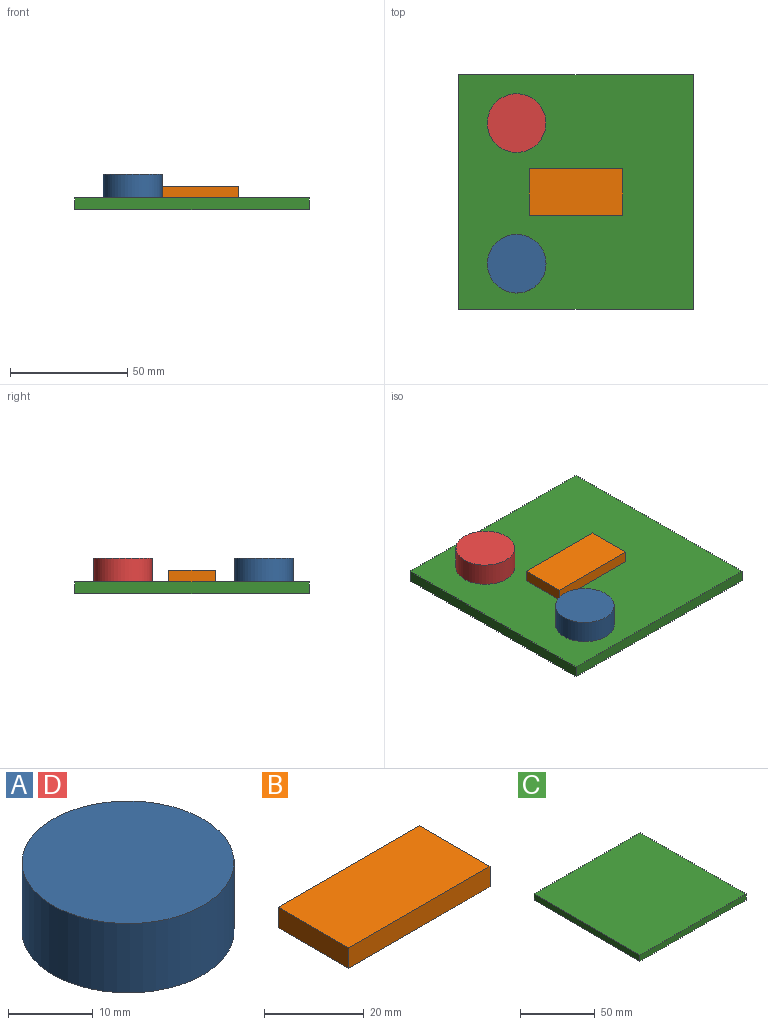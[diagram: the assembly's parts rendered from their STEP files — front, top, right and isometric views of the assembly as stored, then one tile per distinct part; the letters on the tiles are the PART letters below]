
ASSEMBLY  parts=4 mates=3
PART A: 3 faces, bbox 25x25x10 mm
  f0: cylinder r=12.5mm len=25mm, axis (0,0,-1), area 785.4mm2, adj f1,f2
  f1: plane 25x25mm, normal (0,0,1), area 490.9mm2, adj f0
  f2: plane 25x25mm, normal (0,0,-1), area 490.9mm2, adj f0
PART B: 6 faces, bbox 40x20x5 mm
  f0: plane 20x5mm, normal (1,0,0), area 100mm2, adj f1,f3,f4,f5
  f1: plane 40x5mm, normal (0,1,0), area 200mm2, adj f0,f2,f4,f5
  f2: plane 20x5mm, normal (-1,0,0), area 100mm2, adj f1,f3,f4,f5
  f3: plane 40x5mm, normal (0,-1,0), area 200mm2, adj f0,f2,f4,f5
  f4: plane 40x20mm, normal (0,0,1), area 800mm2, adj f0,f1,f2,f3
  f5: plane 40x20mm, normal (0,0,-1), area 800mm2, adj f0,f1,f2,f3
PART C: 6 faces, bbox 100x100x5 mm
  f0: plane 100x5mm, normal (0,-1,0), area 500mm2, adj f1,f3,f4,f5
  f1: plane 100x5mm, normal (1,0,0), area 500mm2, adj f0,f2,f4,f5
  f2: plane 100x5mm, normal (0,1,0), area 500mm2, adj f1,f3,f4,f5
  f3: plane 100x5mm, normal (-1,0,0), area 500mm2, adj f0,f2,f4,f5
  f4: plane 100x100mm, normal (0,0,1), area 10000mm2, adj f0,f1,f2,f3
  f5: plane 100x100mm, normal (0,0,-1), area 10000mm2, adj f0,f1,f2,f3
PART D: same geometry as A
PLACE A t=(-25.32,-30.45,2.72)mm
PLACE B t=(-0.06,0.11,2.72)mm
PLACE C t=(-0.06,0.11,-2.28)mm fixed
PLACE D t=(-25.36,29.45,2.72)mm
MATE planar C.f4 <-> B.f5  axis (0,0,1) through (-0.06,0.11,2.72)mm
MATE planar C.f4 <-> A.f0  axis (0,0,1) through (-0.06,0.11,2.72)mm
MATE planar D.f0 <-> C.f4  axis (0,0,-1) through (-25.36,29.45,2.72)mm
